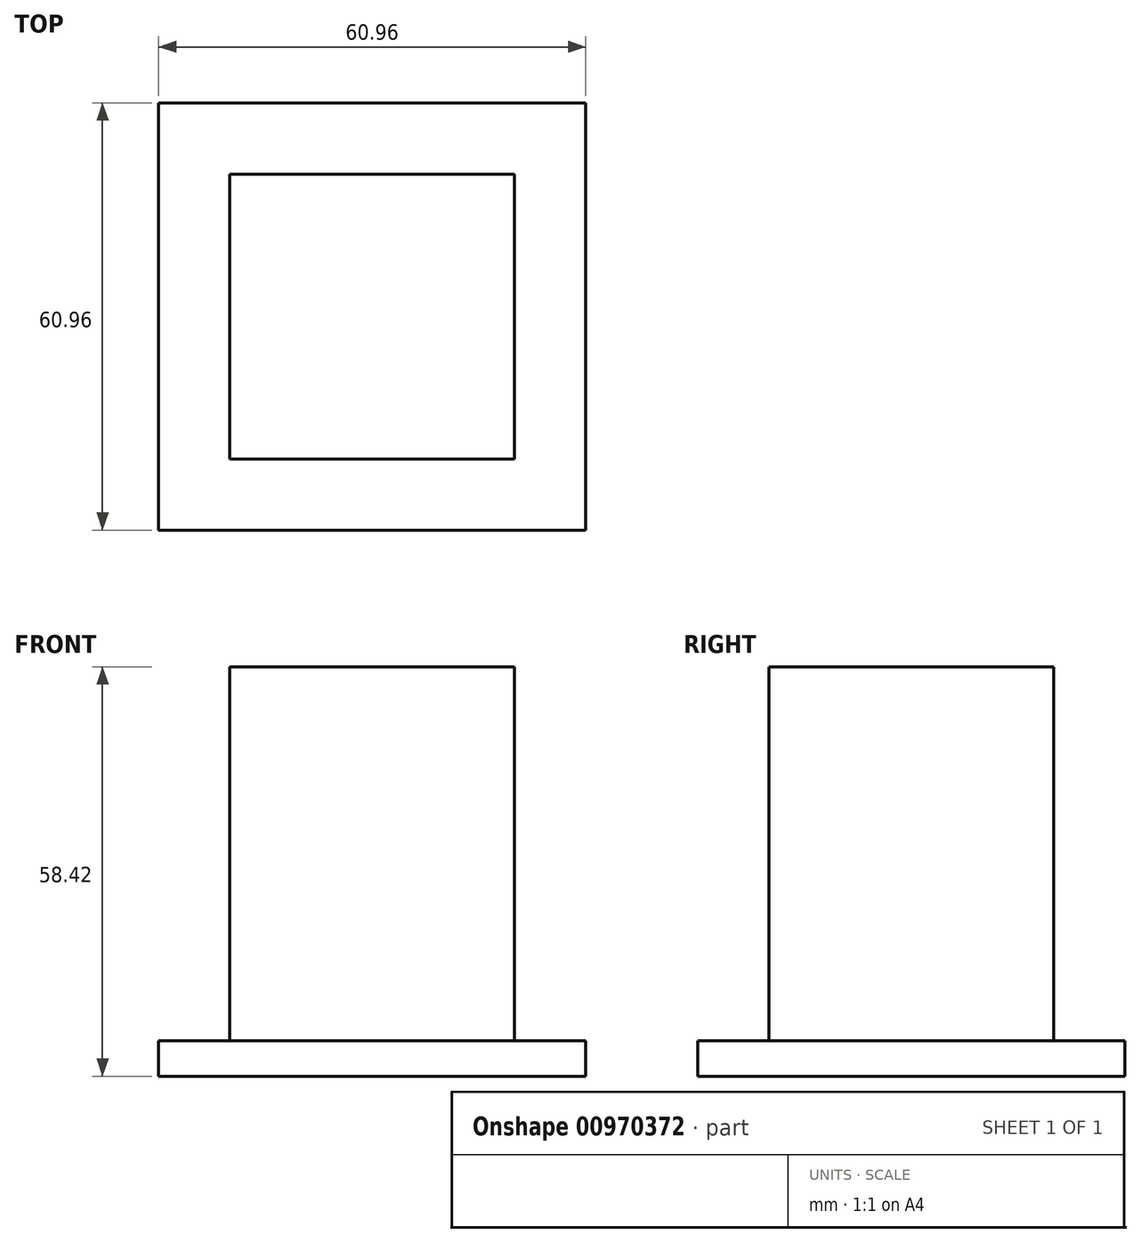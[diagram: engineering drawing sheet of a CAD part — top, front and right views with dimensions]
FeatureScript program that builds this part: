
annotation { "Feature Type Name" : "Feature", "Feature Type Description" : "" }
export const myFeature = defineFeature(function(context is Context, id is Id, definition is map)
    precondition{}
    {
        {
            var Q0;
            Q0=qCreatedBy(makeId("Top.planeOp"),FACE);
            var sketch = newSketch(context, id + "F0", { "sketchPlane" : qUnion([Q0])});
            skLineSegment(sketch, "E0.bottom", {"start": v(0, 0) * mm, "end": v(40.64, 0) * mm});
            skLineSegment(sketch, "E0.top", {"start": v(0, -40.64) * mm, "end": v(40.64, -40.64) * mm});
            skLineSegment(sketch, "E0.left", {"start": v(0, 0) * mm, "end": v(0, -40.64) * mm});
            skLineSegment(sketch, "E0.right", {"start": v(40.64, 0) * mm, "end": v(40.64, -40.64) * mm});
            skSolve(sketch);
        }
        {
            var Q0;
            Q0=makeQuery(id+"F0.imprint","IMPRINT",FACE,{"disambiguationData":[TD([[makeQuery(id+"F0.imprint","IMPRINT",EDGE,{"derivedFrom":sQuery(id+"F0.wireOp",EDGE,"E0.bottom")}),-1.0]])]});
            extrude(context, id + "F1", {"entities" : qUnion([Q0]), "depth" : 58.42 * mm, "offsetDistance" : 25.4 * mm});
        }
        {
            var Q0;
            Q0=qCreatedBy(makeId("Top.planeOp"),FACE);
            var sketch = newSketch(context, id + "F2", { "sketchPlane" : qUnion([Q0])});
            skLineSegment(sketch, "E1.bottom", {"start": v(-10.16, 10.16) * mm, "end": v(50.8, 10.16) * mm});
            skLineSegment(sketch, "E1.top", {"start": v(-10.16, -50.8) * mm, "end": v(50.8, -50.8) * mm});
            skLineSegment(sketch, "E1.left", {"start": v(-10.16, 10.16) * mm, "end": v(-10.16, -50.8) * mm});
            skLineSegment(sketch, "E1.right", {"start": v(50.8, 10.16) * mm, "end": v(50.8, -50.8) * mm});
            skSolve(sketch);
        }
        {
            var Q0;
            Q0 = qSketchRegion(id + "F2", true);
            extrude(context, id + "F3", {"entities" : qUnion([Q0]), "operationType" : NewBodyOperationType.ADD, "depth" : 5.08 * mm, "offsetDistance" : 25.4 * mm});
        }
    });
